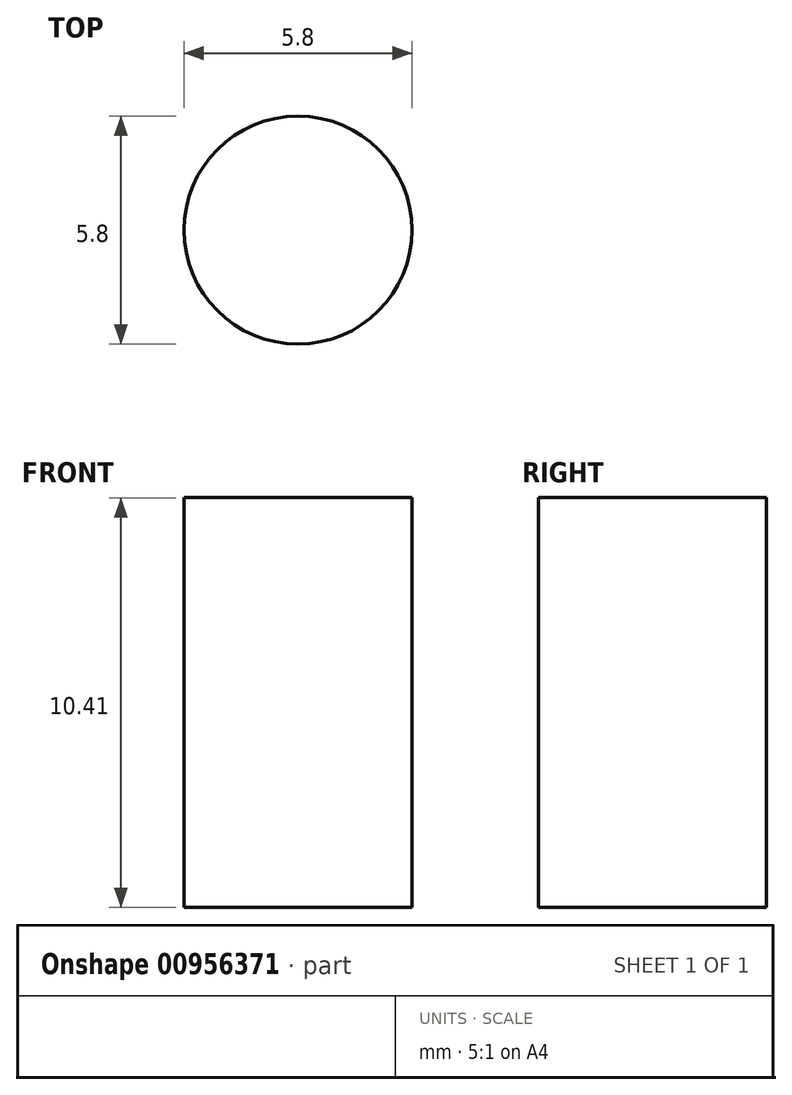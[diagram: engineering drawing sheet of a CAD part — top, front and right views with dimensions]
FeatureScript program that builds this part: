
annotation { "Feature Type Name" : "Feature", "Feature Type Description" : "" }
export const myFeature = defineFeature(function(context is Context, id is Id, definition is map)
    precondition{}
    {
        {
            var Q0;
            Q0=qCreatedBy(makeId("Top.planeOp"),FACE);
            var sketch = newSketch(context, id + "F0", { "sketchPlane" : qUnion([Q0])});
            skCircle(sketch, "E0", {"center": v(0, 0) * mm, "radius": 2.9 * mm});
            skSolve(sketch);
        }
        {
            var Q0;
            Q0=makeQuery(id+"F0.imprint","IMPRINT",FACE,{"disambiguationData":[TD([[makeQuery(id+"F0.imprint","IMPRINT",EDGE,{"derivedFrom":sQuery(id+"F0.wireOp",EDGE,"E0")}),1.0]])]});
            extrude(context, id + "F1", {"entities" : qUnion([Q0]), "depth" : 10.4 * mm, "offsetDistance" : 25.4 * mm});
        }
    });
